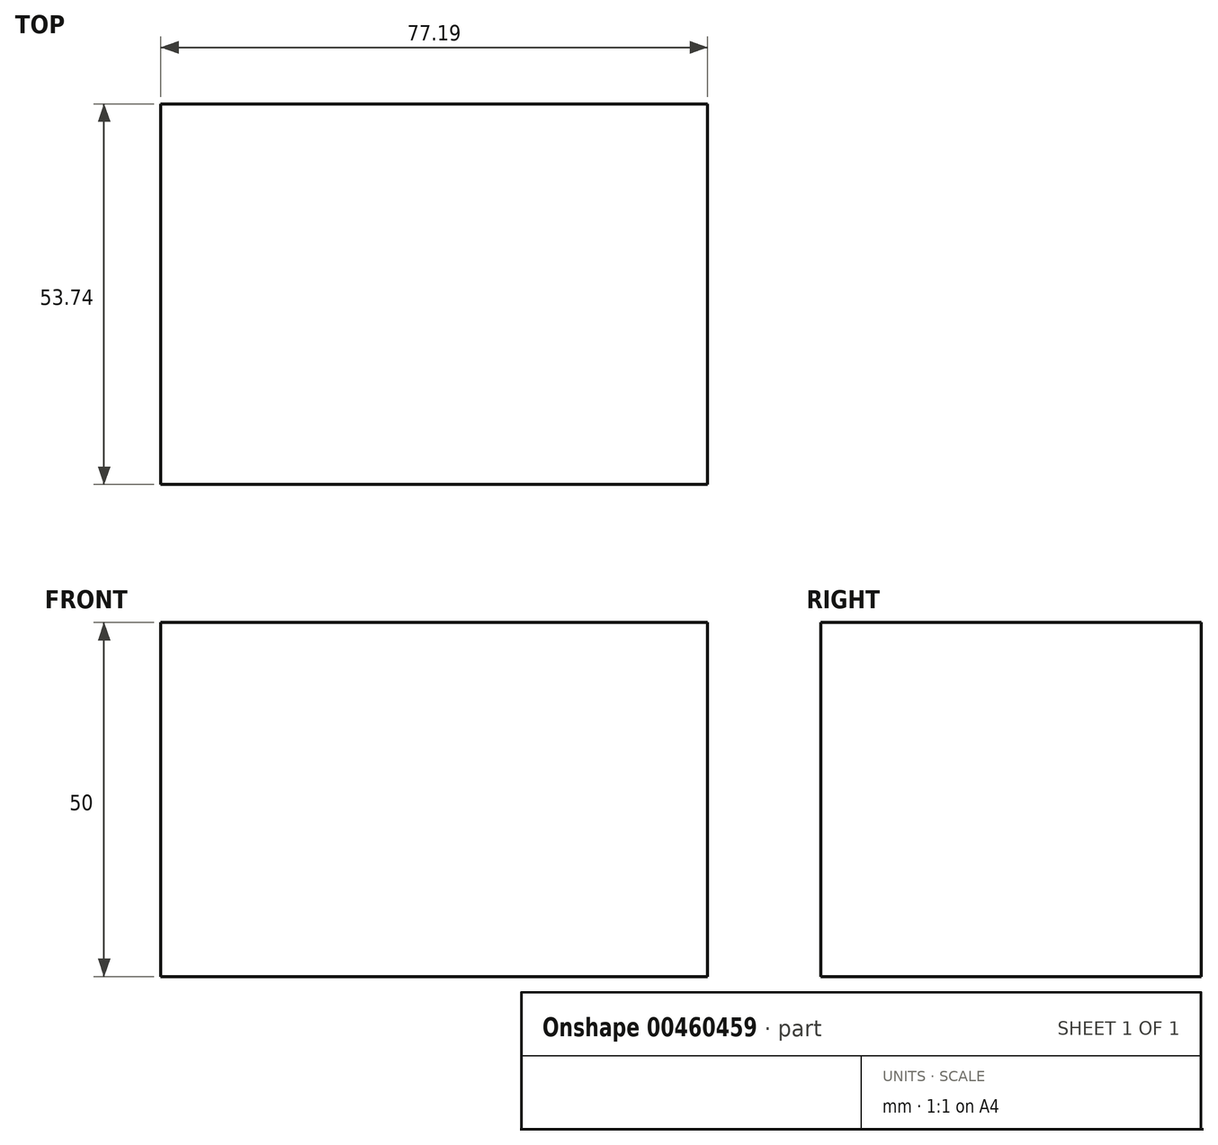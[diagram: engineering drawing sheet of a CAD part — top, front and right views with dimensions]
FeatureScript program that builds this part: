
annotation { "Feature Type Name" : "Feature", "Feature Type Description" : "" }
export const myFeature = defineFeature(function(context is Context, id is Id, definition is map)
    precondition{}
    {
        {
            var Q0;
            Q0=qCreatedBy(makeId("Top.planeOp"),FACE);
            var sketch = newSketch(context, id + "F0", { "sketchPlane" : qUnion([Q0])});
            skLineSegment(sketch, "E0.bottom", {"start": v(-35.1, -26.1) * mm, "end": v(42.09, -26.1) * mm});
            skLineSegment(sketch, "E0.top", {"start": v(-35.1, 27.65) * mm, "end": v(42.09, 27.65) * mm});
            skLineSegment(sketch, "E0.left", {"start": v(-35.1, -26.1) * mm, "end": v(-35.1, 27.65) * mm});
            skLineSegment(sketch, "E0.right", {"start": v(42.09, -26.1) * mm, "end": v(42.09, 27.65) * mm});
            skSolve(sketch);
        }
        {
            var Q0;
            Q0 = qSketchRegion(id + "F0", true);
            extrude(context, id + "F1", {"entities" : qUnion([Q0]), "depth" : 50 * mm});
        }
    });
